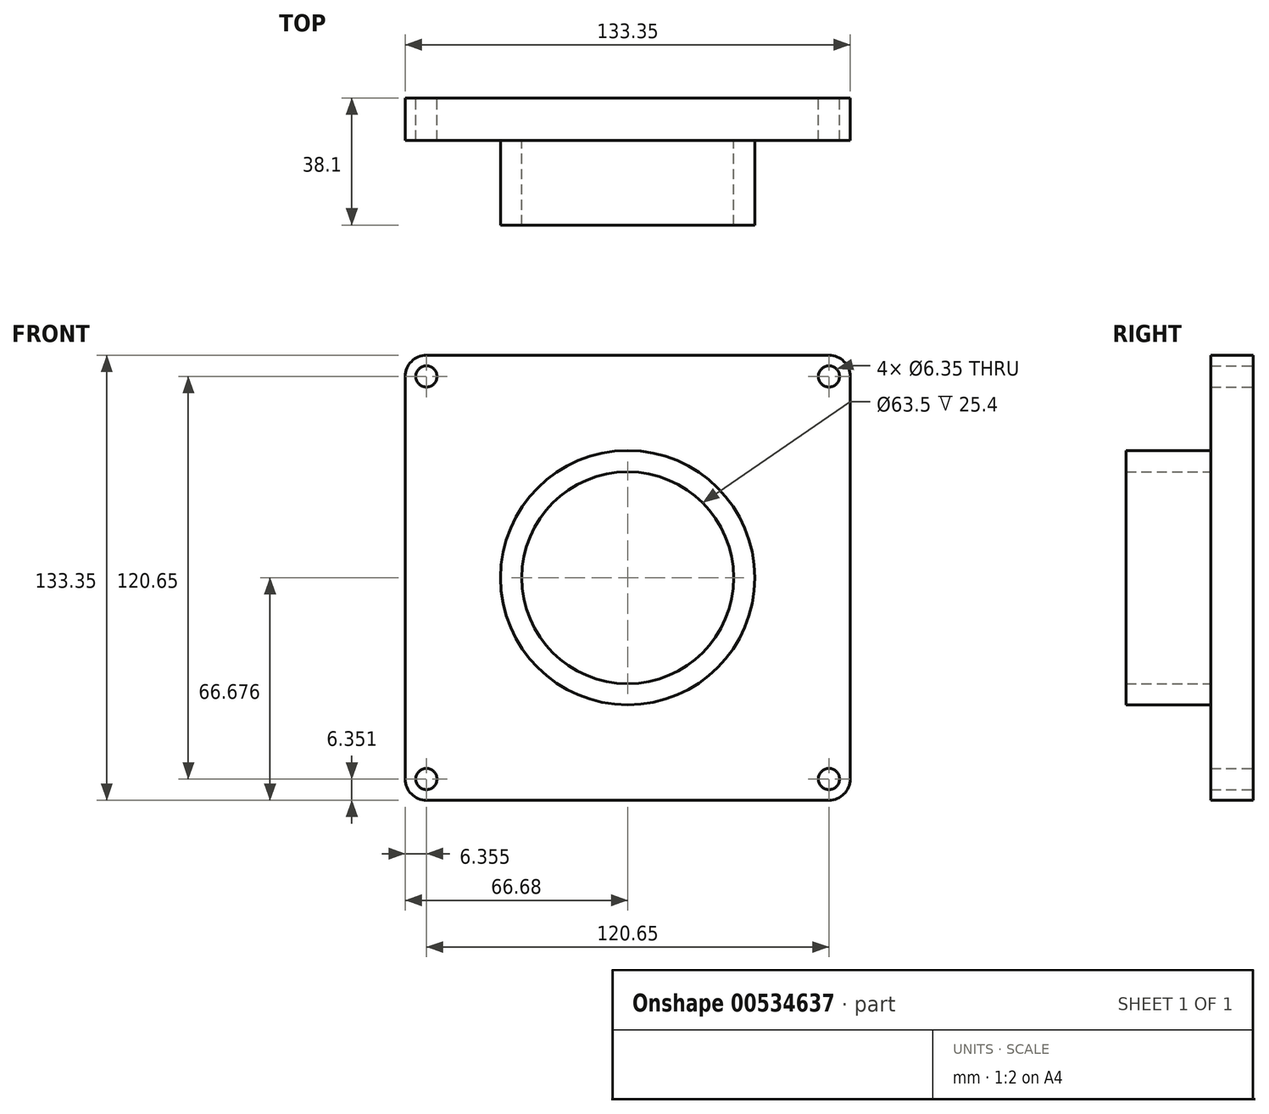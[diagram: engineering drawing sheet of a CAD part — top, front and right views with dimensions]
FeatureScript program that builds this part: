
annotation { "Feature Type Name" : "Feature", "Feature Type Description" : "" }
export const myFeature = defineFeature(function(context is Context, id is Id, definition is map)
    precondition{}
    {
        {
            var Q0;
            Q0=qCreatedBy(makeId("Front.planeOp"),FACE);
            var sketch = newSketch(context, id + "F0", { "sketchPlane" : qUnion([Q0])});
            skLineSegment(sketch, "E0.bottom", {"start": v(-59.87, 68.9) * mm, "end": v(60.78, 68.9) * mm});
            skLineSegment(sketch, "E0.top", {"start": v(-59.87, -64.46) * mm, "end": v(60.78, -64.46) * mm});
            skLineSegment(sketch, "E0.left", {"start": v(-66.22, 62.54) * mm, "end": v(-66.22, -58.1) * mm});
            skLineSegment(sketch, "E0.right", {"start": v(67.13, 62.54) * mm, "end": v(67.13, -58.1) * mm});
            skPoint(sketch, "E1.visualSharp", {"position": v(-66.22, 68.9) * mm});
            skPoint(sketch, "E2.visualSharp", {"position": v(-66.22, -64.46) * mm});
            skArc(sketch, "E2.filletArc", {"start": v(-66.22, -58.1) * mm, "mid": v(-64.36, -62.6) * mm, "end": v(-59.87, -64.46) * mm});
            skPoint(sketch, "E3.visualSharp", {"position": v(67.13, -64.46) * mm});
            skArc(sketch, "E3.filletArc", {"start": v(60.78, -64.46) * mm, "mid": v(65.27, -62.6) * mm, "end": v(67.13, -58.1) * mm});
            skPoint(sketch, "E4.visualSharp", {"position": v(67.13, 68.9) * mm});
            skArc(sketch, "E4.filletArc", {"start": v(67.13, 62.54) * mm, "mid": v(65.27, 67.03) * mm, "end": v(60.78, 68.9) * mm});
            skArc(sketch, "E5.filletArc", {"start": v(-59.87, 68.9) * mm, "mid": v(-64.36, 67.03) * mm, "end": v(-66.22, 62.54) * mm});
            skCircle(sketch, "E6", {"center": v(-59.87, 62.54) * mm, "radius": 3.18 * mm});
            skCircle(sketch, "E7", {"center": v(-59.87, -58.1) * mm, "radius": 3.18 * mm});
            skCircle(sketch, "E8", {"center": v(60.78, -58.1) * mm, "radius": 3.18 * mm});
            skCircle(sketch, "E9", {"center": v(60.78, 62.54) * mm, "radius": 3.18 * mm});
            skSolve(sketch);
        }
        {
            var Q0;
            Q0=makeQuery(id+"F0.imprint","IMPRINT",FACE,{"disambiguationData":[TD([[makeQuery(id+"F0.imprint","IMPRINT",EDGE,{"derivedFrom":sQuery(id+"F0.wireOp",EDGE,"E0.bottom")}),-1.0]])]});
            extrude(context, id + "F1", {"entities" : qUnion([Q0]), "depth" : 12.7 * mm, "offsetDistance" : 25.4 * mm});
        }
        {
            var Q0;
            Q0=makeQuery(id+"F1.opExtrude","CAP_FACE",FACE,{"disambiguationData":[OSD([sQuery(id+"F0.wireOp",EDGE,"E0.bottom"),sQuery(id+"F0.wireOp",EDGE,"E0.top"),sQuery(id+"F0.wireOp",EDGE,"E0.left"),sQuery(id+"F0.wireOp",EDGE,"E0.right"),sQuery(id+"F0.wireOp",EDGE,"E2.filletArc"),sQuery(id+"F0.wireOp",EDGE,"E3.filletArc"),sQuery(id+"F0.wireOp",EDGE,"E4.filletArc"),sQuery(id+"F0.wireOp",EDGE,"E5.filletArc"),sQuery(id+"F0.wireOp",EDGE,"E6"),sQuery(id+"F0.wireOp",EDGE,"E7"),sQuery(id+"F0.wireOp",EDGE,"E8"),sQuery(id+"F0.wireOp",EDGE,"E9")])],"isStart":false});
            var sketch = newSketch(context, id + "F2", { "sketchPlane" : qUnion([Q0])});
            skCircle(sketch, "E10", {"center": v(0.46, 2.22) * mm, "radius": 31.75 * mm});
            skPoint(sketch, "E10.centerSnap0", {"position": v(0.46, -64.46) * mm});
            skCircle(sketch, "E11.0", {"center": v(0.46, 2.22) * mm, "radius": 38.1 * mm});
            skSolve(sketch);
        }
        {
            var Q0;
            Q0=makeQuery(id+"F2.imprint","IMPRINT",FACE,{"disambiguationData":[TD([[makeQuery(id+"F2.imprint","IMPRINT",EDGE,{"derivedFrom":sQuery(id+"F2.wireOp",EDGE,"E10")}),-1.0]])]});
            extrude(context, id + "F3", {"entities" : qUnion([Q0]), "operationType" : NewBodyOperationType.ADD, "depth" : 25.4 * mm, "offsetDistance" : 25.4 * mm});
        }
    });
